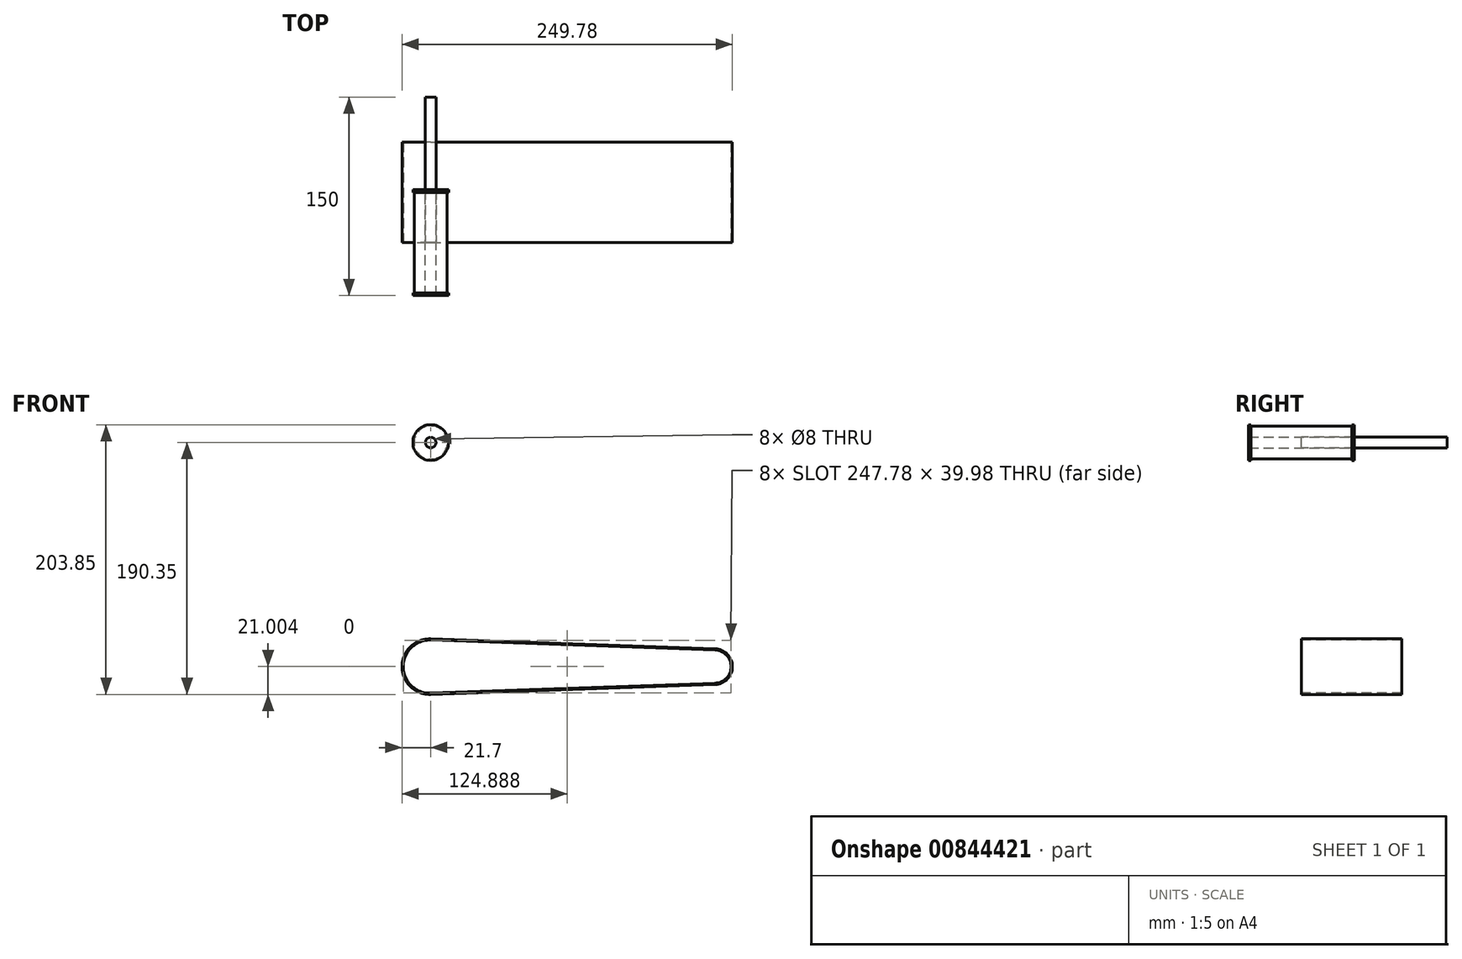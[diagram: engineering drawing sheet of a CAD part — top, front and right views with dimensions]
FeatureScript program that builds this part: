
annotation { "Feature Type Name" : "Feature", "Feature Type Description" : "" }
export const myFeature = defineFeature(function(context is Context, id is Id, definition is map)
    precondition{}
    {
        {
            var Q0;
            Q0=qCreatedBy(makeId("Front.planeOp"),FACE);
            var sketch = newSketch(context, id + "F0", { "sketchPlane" : qUnion([Q0])});
            skCircle(sketch, "E0", {"center": v(0, 0) * mm, "radius": 12.5 * mm});
            skCircle(sketch, "E1", {"center": v(0, 0) * mm, "radius": 13.5 * mm});
            skCircle(sketch, "E2", {"center": v(0, 0) * mm, "radius": 4 * mm});
            skArc(sketch, "E3", {"start": v(0, -149.36) * mm, "mid": v(-20.7, -169.35) * mm, "end": v(0, -189.33) * mm});
            skArc(sketch, "E4", {"start": v(215.01, -181.84) * mm, "mid": v(227.08, -169.35) * mm, "end": v(215.01, -156.85) * mm});
            skLineSegment(sketch, "E5", {"start": v(0, -149.36) * mm, "end": v(215.01, -156.85) * mm});
            skLineSegment(sketch, "E6", {"start": v(0, -189.33) * mm, "end": v(215.01, -181.84) * mm});
            skArc(sketch, "E7.0", {"start": v(0.03, -148.36) * mm, "mid": v(-21.7, -169.35) * mm, "end": v(0.03, -190.33) * mm});
            skLineSegment(sketch, "E7.1", {"start": v(0.03, -148.36) * mm, "end": v(215.05, -155.85) * mm});
            skArc(sketch, "E7.2", {"start": v(215.05, -182.84) * mm, "mid": v(228.08, -169.35) * mm, "end": v(215.05, -155.85) * mm});
            skLineSegment(sketch, "E7.3", {"start": v(0.03, -190.33) * mm, "end": v(215.05, -182.84) * mm});
            skSolve(sketch);
        }
        {
            var Q0;
            Q0=makeQuery(id+"F0.imprint","IMPRINT",FACE,{"disambiguationData":[TD([[makeQuery(id+"F0.imprint","IMPRINT",EDGE,{"derivedFrom":sQuery(id+"F0.wireOp",EDGE,"E0")}),-1.0]])]});
            var Q1;
            Q1=makeQuery(id+"F0.imprint","IMPRINT",FACE,{"disambiguationData":[TD([[makeQuery(id+"F0.imprint","IMPRINT",EDGE,{"derivedFrom":sQuery(id+"F0.wireOp",EDGE,"E0")}),1.0]])]});
            extrude(context, id + "F1", {"entities" : qUnion([Q0, Q1]), "depth" : 80 * mm, "offsetDistance" : 25 * mm, "symmetric" : true});
        }
        {
            var Q0;
            Q0=makeQuery(id+"F0.imprint","IMPRINT",FACE,{"disambiguationData":[TD([[makeQuery(id+"F0.imprint","IMPRINT",EDGE,{"derivedFrom":sQuery(id+"F0.wireOp",EDGE,"E0")}),-1.0]])]});
            extrude(context, id + "F2", {"entities" : qUnion([Q0]), "operationType" : NewBodyOperationType.REMOVE, "depth" : 76 * mm, "offsetDistance" : 25 * mm, "symmetric" : true});
        }
        {
            var Q0;
            Q0=makeQuery(id+"F0.imprint","IMPRINT",FACE,{"disambiguationData":[TD([[makeQuery(id+"F0.imprint","IMPRINT",EDGE,{"derivedFrom":sQuery(id+"F0.wireOp",EDGE,"E3")}),-1.0]])]});
            extrude(context, id + "F3", {"entities" : qUnion([Q0]), "oppositeDirection" : true, "depth" : 76 * mm, "offsetDistance" : 25 * mm});
        }
        {
            var Q0;
            Q0=makeQuery(id+"F0.imprint","IMPRINT",FACE,{"disambiguationData":[TD([[makeQuery(id+"F0.imprint","IMPRINT",EDGE,{"derivedFrom":sQuery(id+"F0.wireOp",EDGE,"E2")}),1.0]])]});
            extrude(context, id + "F4", {"entities" : qUnion([Q0]), "oppositeDirection" : true, "depth" : 110 * mm, "offsetDistance" : 25 * mm});
        }
    });
